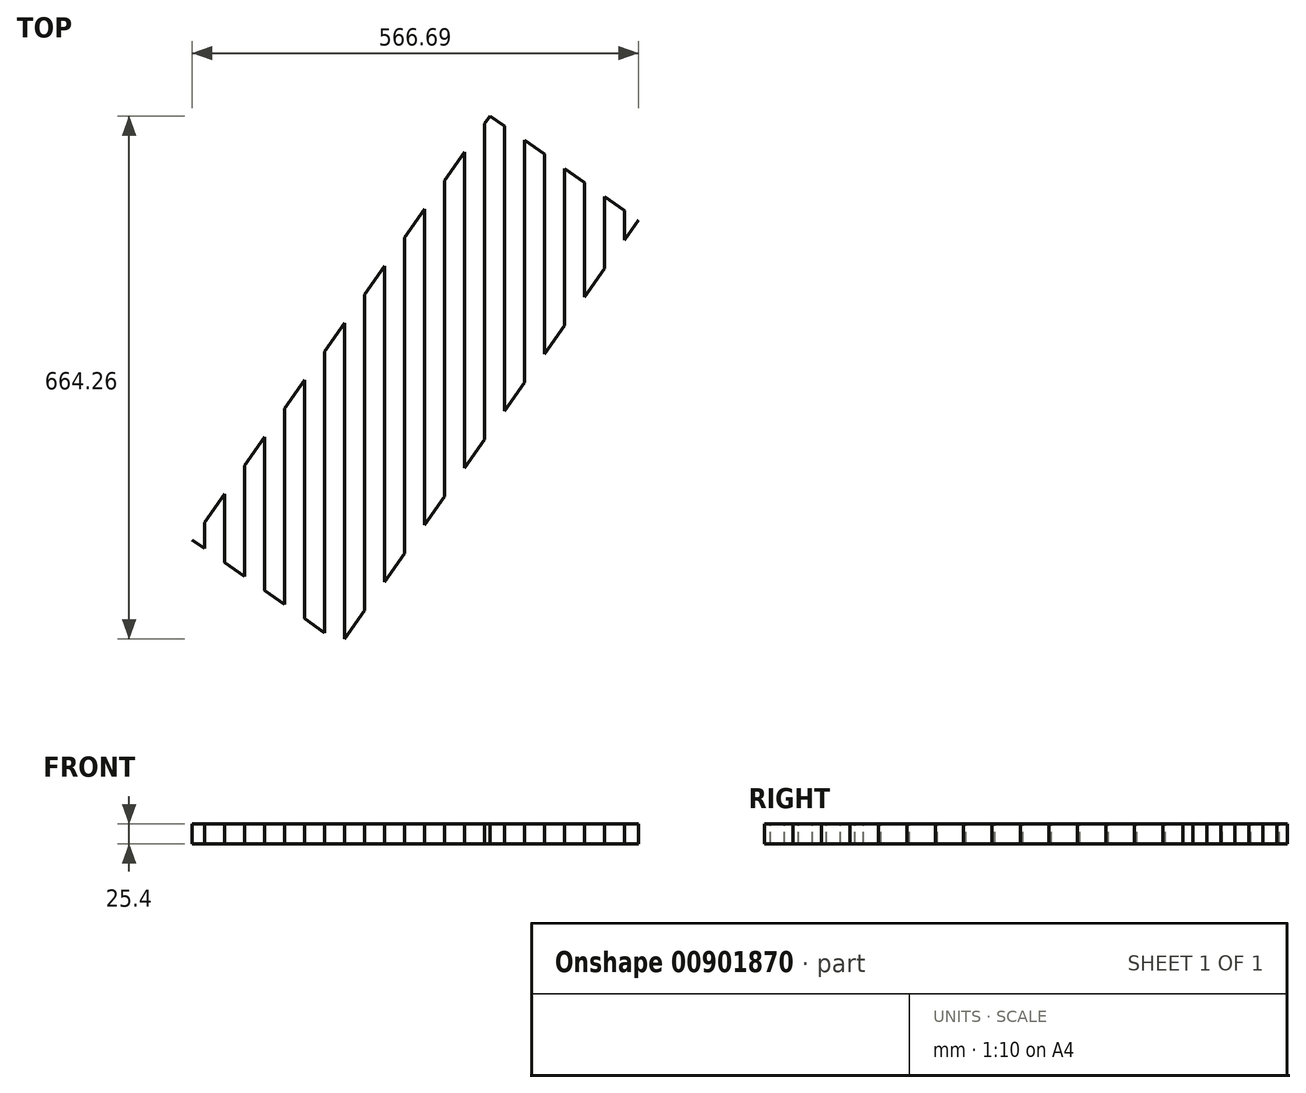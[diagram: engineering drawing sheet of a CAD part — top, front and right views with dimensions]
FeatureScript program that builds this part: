
annotation { "Feature Type Name" : "Feature", "Feature Type Description" : "" }
export const myFeature = defineFeature(function(context is Context, id is Id, definition is map)
    precondition{}
    {
        {
            var Q0;
            Q0=qCreatedBy(makeId("Top.planeOp"),FACE);
            var sketch = newSketch(context, id + "F0", { "sketchPlane" : qUnion([Q0])});
            skLineSegment(sketch, "E0.direction1", {"start": v(0, 0) * mm, "end": v(25.4, 0) * mm, "construction": true});
            skLineSegment(sketch, "E1.0.16.0", {"start": v(406.4, 199.47) * mm, "end": v(406.4, 232.54) * mm});
            skLineSegment(sketch, "E1.0.17.0", {"start": v(431.8, 181.64) * mm, "end": v(431.8, 268.72) * mm});
            skLineSegment(sketch, "E1.0.18.0", {"start": v(457.2, 163.81) * mm, "end": v(457.2, 304.9) * mm});
            skLineSegment(sketch, "E1.0.19.0", {"start": v(482.6, 145.98) * mm, "end": v(482.6, 341.09) * mm});
            skLineSegment(sketch, "E1.0.20.0", {"start": v(508, 128.15) * mm, "end": v(508, 377.27) * mm});
            skLineSegment(sketch, "E1.0.21.0", {"start": v(533.4, 110.32) * mm, "end": v(533.4, 413.45) * mm});
            skLineSegment(sketch, "E1.0.22.0", {"start": v(558.8, 92.49) * mm, "end": v(558.8, 449.63) * mm});
            skLineSegment(sketch, "E1.0.23.0", {"start": v(584.2, 84.62) * mm, "end": v(584.2, 485.81) * mm});
            skLineSegment(sketch, "E1.0.24.0", {"start": v(609.6, 120.8) * mm, "end": v(609.6, 522) * mm});
            skLineSegment(sketch, "E1.0.25.0", {"start": v(635, 156.98) * mm, "end": v(635, 558.17) * mm});
            skLineSegment(sketch, "E1.0.26.0", {"start": v(660.4, 193.16) * mm, "end": v(660.4, 594.36) * mm});
            skLineSegment(sketch, "E1.0.27.0", {"start": v(685.8, 229.34) * mm, "end": v(685.8, 630.54) * mm});
            skLineSegment(sketch, "E1.0.28.0", {"start": v(711.2, 265.52) * mm, "end": v(711.2, 666.72) * mm});
            skLineSegment(sketch, "E1.0.29.0", {"start": v(736.6, 301.7) * mm, "end": v(736.6, 702.9) * mm});
            skLineSegment(sketch, "E2.0.30.0", {"start": v(762, 337.89) * mm, "end": v(762, 739.08) * mm});
            skLineSegment(sketch, "E2.0.31.0", {"start": v(787.4, 374.07) * mm, "end": v(787.4, 735.88) * mm});
            skLineSegment(sketch, "E2.0.32.0", {"start": v(812.8, 410.25) * mm, "end": v(812.8, 718.05) * mm});
            skLineSegment(sketch, "E2.0.33.0", {"start": v(838.2, 446.43) * mm, "end": v(838.2, 700.21) * mm});
            skLineSegment(sketch, "E2.0.34.0", {"start": v(863.6, 482.61) * mm, "end": v(863.6, 682.38) * mm});
            skLineSegment(sketch, "E2.0.35.0", {"start": v(889, 518.8) * mm, "end": v(889, 664.55) * mm});
            skLineSegment(sketch, "E2.0.36.0", {"start": v(914.4, 554.98) * mm, "end": v(914.4, 646.72) * mm});
            skLineSegment(sketch, "E2.0.37.0", {"start": v(939.8, 591.16) * mm, "end": v(939.8, 628.9) * mm});
            skLineSegment(sketch, "E3", {"start": v(406.4, 232.54) * mm, "end": v(431.8, 268.72) * mm});
            skLineSegment(sketch, "E4", {"start": v(768.88, 748.88) * mm, "end": v(787.4, 735.88) * mm});
            skLineSegment(sketch, "E5", {"start": v(957.54, 616.43) * mm, "end": v(939.8, 591.16) * mm});
            skLineSegment(sketch, "E6", {"start": v(558.8, 92.49) * mm, "end": v(533.4, 110.32) * mm});
            skLineSegment(sketch, "E7.trimOffspring", {"start": v(406.4, 199.47) * mm, "end": v(390.85, 210.4) * mm});
            skLineSegment(sketch, "E8.trimOffspring", {"start": v(457.2, 304.9) * mm, "end": v(482.6, 341.09) * mm});
            skLineSegment(sketch, "E9.trimOffspring", {"start": v(508, 377.27) * mm, "end": v(533.4, 413.45) * mm});
            skLineSegment(sketch, "E10.trimOffspring", {"start": v(558.8, 449.63) * mm, "end": v(584.2, 485.81) * mm});
            skLineSegment(sketch, "E11.trimOffspring", {"start": v(609.6, 522) * mm, "end": v(635, 558.17) * mm});
            skLineSegment(sketch, "E12.trimOffspring", {"start": v(660.4, 594.36) * mm, "end": v(685.8, 630.54) * mm});
            skLineSegment(sketch, "E13.trimOffspring", {"start": v(711.2, 666.72) * mm, "end": v(736.6, 702.9) * mm});
            skLineSegment(sketch, "E14.trimOffspring", {"start": v(762, 739.08) * mm, "end": v(768.88, 748.88) * mm});
            skLineSegment(sketch, "E15.trimOffspring", {"start": v(457.2, 163.81) * mm, "end": v(431.8, 181.64) * mm});
            skLineSegment(sketch, "E16.trimOffspring", {"start": v(508, 128.15) * mm, "end": v(482.6, 145.98) * mm});
            skLineSegment(sketch, "E17.trimOffspring", {"start": v(609.6, 120.8) * mm, "end": v(584.2, 84.62) * mm});
            skLineSegment(sketch, "E18.trimOffspring", {"start": v(660.4, 193.16) * mm, "end": v(635, 156.98) * mm});
            skLineSegment(sketch, "E19.trimOffspring", {"start": v(711.2, 265.52) * mm, "end": v(685.8, 229.34) * mm});
            skLineSegment(sketch, "E20.trimOffspring", {"start": v(762, 337.89) * mm, "end": v(736.6, 301.7) * mm});
            skLineSegment(sketch, "E21.trimOffspring", {"start": v(812.8, 410.25) * mm, "end": v(787.4, 374.07) * mm});
            skLineSegment(sketch, "E22.trimOffspring", {"start": v(863.6, 482.61) * mm, "end": v(838.2, 446.43) * mm});
            skLineSegment(sketch, "E23.trimOffspring", {"start": v(914.4, 554.98) * mm, "end": v(889, 518.8) * mm});
            skLineSegment(sketch, "E24.trimOffspring", {"start": v(812.8, 718.05) * mm, "end": v(838.2, 700.21) * mm});
            skLineSegment(sketch, "E25.trimOffspring", {"start": v(863.6, 682.38) * mm, "end": v(889, 664.55) * mm});
            skLineSegment(sketch, "E26.trimOffspring", {"start": v(914.4, 646.72) * mm, "end": v(939.8, 628.9) * mm});
            skSolve(sketch);
        }
        {
            var Q0;
            Q0=sQuery(id+"F0.wireOp",EDGE,"E25.trimOffspring");
            var Q1;
            Q1=sQuery(id+"F0.wireOp",EDGE,"E1.0.18.0");
            var Q2;
            Q2=sQuery(id+"F0.wireOp",EDGE,"E4");
            var Q3;
            Q3=sQuery(id+"F0.wireOp",EDGE,"E1.0.23.0");
            var Q4;
            Q4=sQuery(id+"F0.wireOp",EDGE,"E8.trimOffspring");
            var Q5;
            Q5=sQuery(id+"F0.wireOp",EDGE,"E1.0.19.0");
            var Q6;
            Q6=sQuery(id+"F0.wireOp",EDGE,"E26.trimOffspring");
            var Q7;
            Q7=sQuery(id+"F0.wireOp",EDGE,"E22.trimOffspring");
            var Q8;
            Q8=sQuery(id+"F0.wireOp",EDGE,"E1.0.22.0");
            var Q9;
            Q9=sQuery(id+"F0.wireOp",EDGE,"E24.trimOffspring");
            var Q10;
            Q10=sQuery(id+"F0.wireOp",EDGE,"E2.0.37.0");
            var Q11;
            Q11=sQuery(id+"F0.wireOp",EDGE,"E1.0.29.0");
            var Q12;
            Q12=sQuery(id+"F0.wireOp",EDGE,"E1.0.21.0");
            var Q13;
            Q13=sQuery(id+"F0.wireOp",EDGE,"E2.0.32.0");
            var Q14;
            Q14=sQuery(id+"F0.wireOp",EDGE,"E1.0.16.0");
            var Q15;
            Q15=sQuery(id+"F0.wireOp",EDGE,"E17.trimOffspring");
            var Q16;
            Q16=sQuery(id+"F0.wireOp",EDGE,"E2.0.31.0");
            var Q17;
            Q17=sQuery(id+"F0.wireOp",EDGE,"E2.0.36.0");
            var Q18;
            Q18=sQuery(id+"F0.wireOp",EDGE,"E19.trimOffspring");
            var Q19;
            Q19=sQuery(id+"F0.wireOp",EDGE,"E5");
            var Q20;
            Q20=sQuery(id+"F0.wireOp",EDGE,"E3");
            var Q21;
            Q21=sQuery(id+"F0.wireOp",EDGE,"E20.trimOffspring");
            var Q22;
            Q22=sQuery(id+"F0.wireOp",EDGE,"E12.trimOffspring");
            var Q23;
            Q23=sQuery(id+"F0.wireOp",EDGE,"E2.0.33.0");
            var Q24;
            Q24=sQuery(id+"F0.wireOp",EDGE,"E1.0.24.0");
            var Q25;
            Q25=sQuery(id+"F0.wireOp",EDGE,"E2.0.35.0");
            var Q26;
            Q26=sQuery(id+"F0.wireOp",EDGE,"E2.0.30.0");
            var Q27;
            Q27=sQuery(id+"F0.wireOp",EDGE,"E15.trimOffspring");
            var Q28;
            Q28=sQuery(id+"F0.wireOp",EDGE,"E11.trimOffspring");
            var Q29;
            Q29=sQuery(id+"F0.wireOp",EDGE,"E1.0.28.0");
            var Q30;
            Q30=sQuery(id+"F0.wireOp",EDGE,"E16.trimOffspring");
            var Q31;
            Q31=sQuery(id+"F0.wireOp",EDGE,"E1.0.25.0");
            var Q32;
            Q32=sQuery(id+"F0.wireOp",EDGE,"E1.0.20.0");
            var Q33;
            Q33=sQuery(id+"F0.wireOp",EDGE,"E7.trimOffspring");
            var Q34;
            Q34=sQuery(id+"F0.wireOp",EDGE,"E9.trimOffspring");
            var Q35;
            Q35=sQuery(id+"F0.wireOp",EDGE,"E13.trimOffspring");
            var Q36;
            Q36=sQuery(id+"F0.wireOp",EDGE,"E2.0.34.0");
            var Q37;
            Q37=sQuery(id+"F0.wireOp",EDGE,"E1.0.17.0");
            var Q38;
            Q38=sQuery(id+"F0.wireOp",EDGE,"E23.trimOffspring");
            var Q39;
            Q39=sQuery(id+"F0.wireOp",EDGE,"E1.0.26.0");
            var Q40;
            Q40=sQuery(id+"F0.wireOp",EDGE,"E1.0.27.0");
            var Q41;
            Q41=sQuery(id+"F0.wireOp",EDGE,"E18.trimOffspring");
            var Q42;
            Q42=sQuery(id+"F0.wireOp",EDGE,"E21.trimOffspring");
            var Q43;
            Q43=sQuery(id+"F0.wireOp",EDGE,"E6");
            var Q44;
            Q44=sQuery(id+"F0.wireOp",EDGE,"E10.trimOffspring");
            var Q45;
            Q45=sQuery(id+"F0.wireOp",EDGE,"E14.trimOffspring");
            extrude(context, id + "F1", {"bodyType" : ToolBodyType.SURFACE, "surfaceEntities" : qUnion([Q0, Q1, Q2, Q3, Q4, Q5, Q6, Q7, Q8, Q9, Q10, Q11, Q12, Q13, Q14, Q15, Q16, Q17, Q18, Q19, Q20, Q21, Q22, Q23, Q24, Q25, Q26, Q27, Q28, Q29, Q30, Q31, Q32, Q33, Q34, Q35, Q36, Q37, Q38, Q39, Q40, Q41, Q42, Q43, Q44, Q45]), "depth" : 25.4 * mm, "offsetDistance" : 25.4 * mm});
        }
    });
